# Revit family: NAU_Naughtone_Stng_Polly_StoolSledBase----
name_source: partatom
category: Furniture
revit_build: Autodesk Revit 2016 (Build: 20150220_1215(x64)
units: mm (PartAtom-declared; Revit-internal decimal feet)

## family parameters
Always vertical = Yes
Cut with Voids When Loaded = No
OmniClass Number = 23.40.20.00
OmniClass Title = General Furniture and Specialties
Room Calculation Point = No
Shared = Yes
Work Plane-Based = No

## types (2) — shared parameters
AssetType = Movable
CodePerformance = Pr_40_50_12 : Chairs, seats and benches
Color = Various
DurationUnit = year
ExpectedLife = 5
IfcExportAs = IfcFurnishingElementType
IfcExportType = CHAIR
Keynote = Pr_40_50_12
MainColor = Various
ManufacturerAddress = Knaresborough Tech Park, Manse Lane, Knaresborough, HG5 8LF
ManufacturerName = Naughtone
ManufacturerURL = www.naughtone.com
Material = Polypropylene, Steel
NBSDescription = Seating
NBSReference = 45-35-72/352
NominalLength = 565 mm  [stored 1.85367 ft]
NominalWidth = 565 mm  [stored 1.85367 ft]
ProductInformation = www.naughtone.com/products/polly/
Revision = 1
Shape = Rectangular
SustainabilityPerformance = FSC certified, SCS indoor advantage gold
URL = www.naughtone.com
Uniclass2015Code = Pr_40_50_12
Uniclass2015Title = Chairs, seats and benches
Uniclass2015Version = Products v1.10
Version = 1
WarrantyDescription = 5 Years
WarrantyDurationLabor = 5
WarrantyDurationParts = 5
WarrantyDurationUnit = year

## per-type parameters (varying)
| type | Description | Finish | IsBarStoolSledBase | IsCounterHeightStoolSledBase | Model | ModelNumber | ModelReference | NominalHeight | Seating | Size |
| Polly Barstool Sled Base POLLYBSBSL 565 x 565 x 1100mm | Polly Barstool Sled Base | Match finish options on current Polly models. Available in 8 x RAL colours | Yes | No | POLLYBSBSL | POLLYBSBSL | Polly Barstool Sled Base | 1100 mm | 655 mm  [stored 2.14895 ft] | 565 x 565 x 1100mm |
| Polly Counter Height Stool Sled Base POLLYCHSBSL 565 x 565 x 1005mm | Polly Counter Height Stool Sled Base | Polypropylene, Steel | No | Yes | POLLYCHSBSL | POLLYCHSBSL | Polly Counter Height Stool Sled Base | 1005 mm  [stored 3.29724 ft] | 745 mm  [stored 2.44423 ft] | 565 x 565 x 1005mm |

note: [stored X ft] marks values corroborated as IEEE doubles in the binary element streams (Revit-internal decimal feet)

## geometry (parser evidence)
native form markers: Sweep x4
no freeform markers — native parametric forms only
